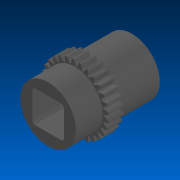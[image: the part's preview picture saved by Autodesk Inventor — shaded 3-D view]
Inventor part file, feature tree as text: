
AUTODESK INVENTOR PART (.ipt)
format: ipt  version: 2022.2 (Build 262287000, 287)  size: 319,488 bytes
history: native  units: in
note: dims shown in document units (in); Inventor stores cm internally (conversion verified against a paired STEP export)
features: fillet x1
ambient origin geometry x8: Origin, YZ Plane, XZ Plane, XY Plane, X Axis, Y Axis, Z Axis, Center Point
bodies: Solid1 (feature_tree)
feature tree (1):
  fillet  "Fillet1"  [1 undecoded]
note: 1 required parameter value undecoded (feature->parameter linkage not recoverable at this tier; creation-order binding heuristic only, values carry confidence <= 0.55)
